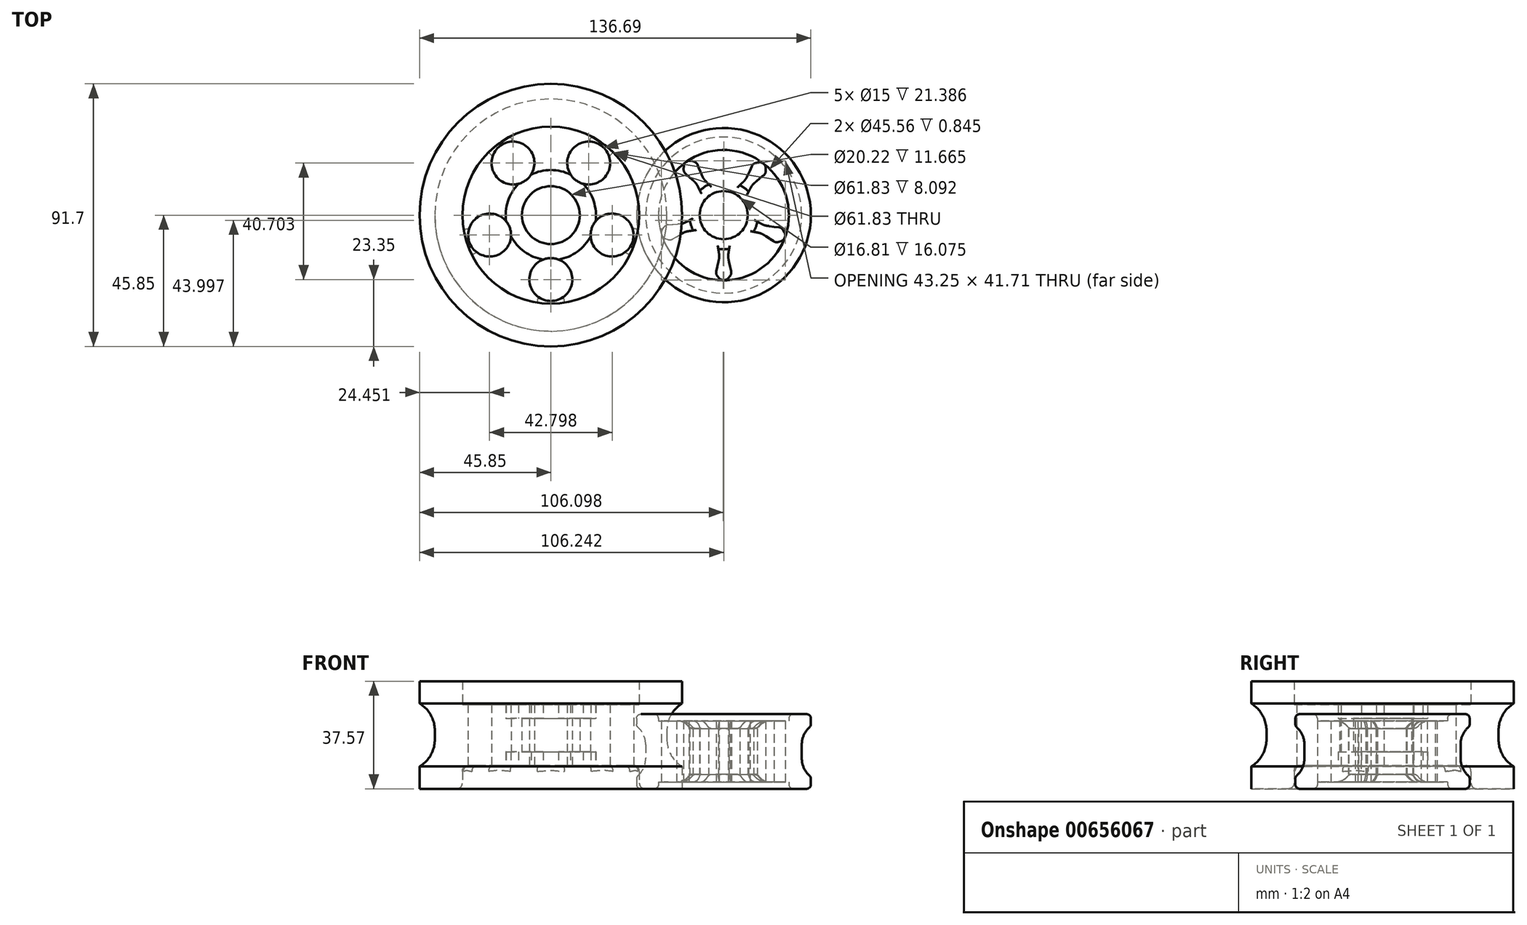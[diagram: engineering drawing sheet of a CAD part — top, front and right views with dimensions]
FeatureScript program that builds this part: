
annotation { "Feature Type Name" : "Feature", "Feature Type Description" : "" }
export const myFeature = defineFeature(function(context is Context, id is Id, definition is map)
    precondition{}
    {
        {
            var Q0;
            Q0=qCreatedBy(makeId("Front.planeOp"),FACE);
            var sketch = newSketch(context, id + "F0", { "sketchPlane" : qUnion([Q0])});
            skLineSegment(sketch, "E0", {"start": v(29.95, 21.08) * mm, "end": v(33.1, 21.08) * mm});
            skLineSegment(sketch, "E1", {"start": v(33.1, 21.08) * mm, "end": v(33.1, 5) * mm});
            skLineSegment(sketch, "E2", {"start": v(33.1, 5) * mm, "end": v(29.95, 5) * mm});
            skLineSegment(sketch, "E3", {"start": v(29.95, 5) * mm, "end": v(29.95, 0) * mm});
            skLineSegment(sketch, "E4", {"start": v(29.95, 0) * mm, "end": v(37.61, 0) * mm});
            skLineSegment(sketch, "E5", {"start": v(37.61, 0) * mm, "end": v(37.61, 2.35) * mm});
            skLineSegment(sketch, "E6", {"start": v(37.61, 2.35) * mm, "end": v(48.45, 2.35) * mm});
            skLineSegment(sketch, "E7", {"start": v(48.45, 2.35) * mm, "end": v(48.45, 5) * mm});
            skLineSegment(sketch, "E8", {"start": v(48.45, 5) * mm, "end": v(51.99, 5) * mm});
            skLineSegment(sketch, "E9", {"start": v(33.1, 13.04) * mm, "end": v(60.4, 13.04) * mm, "construction": true});
            skLineSegment(sketch, "E10.MirrorCS", {"start": v(37.61, 23.73) * mm, "end": v(48.45, 23.73) * mm});
            skLineSegment(sketch, "E11.MirrorCS", {"start": v(48.45, 21.08) * mm, "end": v(51.99, 21.08) * mm});
            skLineSegment(sketch, "E12.MirrorCS", {"start": v(48.45, 23.73) * mm, "end": v(48.45, 21.08) * mm});
            skLineSegment(sketch, "E13.MirrorCS", {"start": v(37.61, 26.08) * mm, "end": v(37.61, 23.73) * mm});
            skLineSegment(sketch, "E14.MirrorCS", {"start": v(29.95, 26.08) * mm, "end": v(37.61, 26.08) * mm});
            skLineSegment(sketch, "E15.MirrorCS", {"start": v(29.95, 21.08) * mm, "end": v(29.95, 26.08) * mm});
            skLineSegment(sketch, "E16", {"start": v(51.99, 21.08) * mm, "end": v(51.99, 5) * mm});
            skLineSegment(sketch, "E17", {"start": v(60.4, -28.23) * mm, "end": v(60.4, 48.4) * mm, "construction": true});
            skSolve(sketch);
        }
        {
            var Q0;
            Q0=makeQuery(id+"F0.imprint","IMPRINT",FACE,{"disambiguationData":[TD([[makeQuery(id+"F0.imprint","IMPRINT",EDGE,{"derivedFrom":sQuery(id+"F0.wireOp",EDGE,"E0")}),1.0]])]});
            var Q1;
            Q1=sQuery(id+"F0.wireOp",EDGE,"E17");
            revolve(context, id + "F1", {"entities" : qUnion([Q0]), "axis" : qUnion([Q1]), "revolveType" : RevolveType.FULL});
        }
        {
            var Q0;
            Q0=makeQuery(id+"F1.opRevolve","SWEPT_EDGE",EDGE,{"disambiguationData":[OSD([sQuery(id+"F0.wireOp",EDGE,"E0"),sQuery(id+"F0.wireOp",EDGE,"E15.MirrorCS")])]});
            var Q1;
            Q1=makeQuery(id+"F1.opRevolve","SWEPT_EDGE",EDGE,{"disambiguationData":[OSD([sQuery(id+"F0.wireOp",EDGE,"E14.MirrorCS"),sQuery(id+"F0.wireOp",EDGE,"E15.MirrorCS")])]});
            var Q2;
            Q2=makeQuery(id+"F1.opRevolve","SWEPT_EDGE",EDGE,{"disambiguationData":[OSD([sQuery(id+"F0.wireOp",EDGE,"E2"),sQuery(id+"F0.wireOp",EDGE,"E3")])]});
            var Q3;
            Q3=makeQuery(id+"F1.opRevolve","SWEPT_EDGE",EDGE,{"disambiguationData":[OSD([sQuery(id+"F0.wireOp",EDGE,"E3"),sQuery(id+"F0.wireOp",EDGE,"E4")])]});
            var Q4;
            Q4=makeQuery(id+"F1.opRevolve","SWEPT_EDGE",EDGE,{"disambiguationData":[OSD([sQuery(id+"F0.wireOp",EDGE,"E4"),sQuery(id+"F0.wireOp",EDGE,"E5")])]});
            var Q5;
            Q5=makeQuery(id+"F1.opRevolve","SWEPT_EDGE",EDGE,{"disambiguationData":[OSD([sQuery(id+"F0.wireOp",EDGE,"E13.MirrorCS"),sQuery(id+"F0.wireOp",EDGE,"E14.MirrorCS")])]});
            fillet(context, id + "F2", {"entities" : qUnion([Q0, Q1, Q2, Q3, Q4, Q5]), "radius" : 1.5 * mm, "tangentPropagation" : true, "allowEdgeOverflow" : false});
        }
        {
            var Q0;
            Q0=makeQuery(id+"F1.opRevolve","SWEPT_EDGE",EDGE,{"disambiguationData":[OSD([sQuery(id+"F0.wireOp",EDGE,"E1"),sQuery(id+"F0.wireOp",EDGE,"E2")])]});
            var Q1;
            Q1=makeQuery(id+"F1.opRevolve","SWEPT_EDGE",EDGE,{"disambiguationData":[OSD([sQuery(id+"F0.wireOp",EDGE,"E0"),sQuery(id+"F0.wireOp",EDGE,"E1")])]});
            fillet(context, id + "F3", {"entities" : qUnion([Q0, Q1]), "radius" : 8 * mm, "tangentPropagation" : true, "allowEdgeOverflow" : false});
        }
        {
            var Q0;
            Q0=qCreatedBy(makeId("Top.planeOp"),FACE);
            var sketch = newSketch(context, id + "F4", { "sketchPlane" : qUnion([Q0])});
            skArc(sketch, "E18", {"start": v(58.5, -11.8) * mm, "mid": v(60.4, -11.95) * mm, "end": v(62.29, -11.8) * mm});
            skLineSegment(sketch, "E19", {"start": v(60.4, 0) * mm, "end": v(60.4, -26.79) * mm, "construction": true});
            skLineSegment(sketch, "E20", {"start": v(58.5, -11.8) * mm, "end": v(58.78, -13.59) * mm});
            skLineSegment(sketch, "E21", {"start": v(58.73, -15.4) * mm, "end": v(58.2, -17.86) * mm});
            skLineSegment(sketch, "E22", {"start": v(58.18, -21.25) * mm, "end": v(58.77, -21.98) * mm});
            skLineSegment(sketch, "E23", {"start": v(58.15, -18.08) * mm, "end": v(57.79, -19.48) * mm});
            skLineSegment(sketch, "E24", {"start": v(60.32, -22.7) * mm, "end": v(60.4, -22.7) * mm});
            skPoint(sketch, "E25.visualSharp", {"position": v(59.37, -22.7) * mm});
            skArc(sketch, "E25.filletArc", {"start": v(58.77, -21.98) * mm, "mid": v(59.46, -22.52) * mm, "end": v(60.32, -22.7) * mm});
            skPoint(sketch, "E26.visualSharp", {"position": v(57.53, -20.46) * mm});
            skArc(sketch, "E26.filletArc", {"start": v(57.79, -19.48) * mm, "mid": v(57.77, -20.4) * mm, "end": v(58.18, -21.25) * mm});
            skPoint(sketch, "E27.visualSharp", {"position": v(58.92, -14.5) * mm});
            skArc(sketch, "E27.filletArc", {"start": v(58.73, -15.4) * mm, "mid": v(58.83, -14.5) * mm, "end": v(58.78, -13.59) * mm});
            skLineSegment(sketch, "E28.MirrorCS", {"start": v(60.46, -22.7) * mm, "end": v(60.4, -22.7) * mm});
            skLineSegment(sketch, "E29.MirrorCS", {"start": v(62.6, -21.25) * mm, "end": v(62.01, -21.98) * mm});
            skArc(sketch, "E30.MirrorCS", {"start": v(63, -19.48) * mm, "mid": v(63.01, -20.4) * mm, "end": v(62.6, -21.25) * mm});
            skArc(sketch, "E31.MirrorCS", {"start": v(62.01, -21.98) * mm, "mid": v(61.32, -22.52) * mm, "end": v(60.46, -22.7) * mm});
            skArc(sketch, "E32.MirrorCS", {"start": v(62.06, -15.4) * mm, "mid": v(61.95, -14.5) * mm, "end": v(62, -13.59) * mm});
            skLineSegment(sketch, "E33.MirrorCS", {"start": v(62.06, -15.4) * mm, "end": v(62.6, -17.97) * mm});
            skLineSegment(sketch, "E34.MirrorCS", {"start": v(62.29, -11.8) * mm, "end": v(62, -13.59) * mm});
            skLineSegment(sketch, "E35.MirrorCS", {"start": v(62.6, -17.97) * mm, "end": v(63, -19.48) * mm});
            skPoint(sketch, "E36.MirrorP", {"position": v(61.87, -14.5) * mm});
            skPoint(sketch, "E37.MirrorP", {"position": v(63.25, -20.46) * mm});
            skPoint(sketch, "E38.MirrorP", {"position": v(61.41, -22.7) * mm});
            skPoint(sketch, "E39.visualSharp", {"position": v(58.18, -17.97) * mm});
            skArc(sketch, "E39.filletArc", {"start": v(58.15, -18.08) * mm, "mid": v(58.18, -17.97) * mm, "end": v(58.2, -17.86) * mm});
            skCircle(sketch, "E40", {"center": v(60.4, 0) * mm, "radius": 11.95 * mm, "construction": true});
            skLineSegment(sketch, "E41.1.0", {"start": v(48.57, -1.74) * mm, "end": v(46.95, -2.55) * mm});
            skLineSegment(sketch, "E41.1.1", {"start": v(42.47, -3.3) * mm, "end": v(41.03, -3.37) * mm});
            skLineSegment(sketch, "E41.1.2", {"start": v(45.2, -3.04) * mm, "end": v(42.7, -3.28) * mm});
            skPoint(sketch, "E41.1.3", {"position": v(41.74, -8.88) * mm});
            skArc(sketch, "E41.1.4", {"start": v(48.57, -1.74) * mm, "mid": v(49, -3.6) * mm, "end": v(49.71, -5.35) * mm});
            skPoint(sketch, "E41.1.5", {"position": v(42.58, -3.3) * mm});
            skLineSegment(sketch, "E41.1.6", {"start": v(43.91, -7.51) * mm, "end": v(42.6, -8.34) * mm});
            skLineSegment(sketch, "E41.1.7", {"start": v(46.2, -6.22) * mm, "end": v(43.91, -7.51) * mm});
            skPoint(sketch, "E41.1.8", {"position": v(39.04, -7.8) * mm});
            skPoint(sketch, "E41.1.9", {"position": v(38.43, -5.86) * mm});
            skLineSegment(sketch, "E41.1.10", {"start": v(49.71, -5.35) * mm, "end": v(47.92, -5.63) * mm});
            skPoint(sketch, "E41.1.11", {"position": v(47, -5.77) * mm});
            skPoint(sketch, "E41.1.12", {"position": v(46.12, -2.95) * mm});
            skPoint(sketch, "E41.1.13", {"position": v(40.02, -3.43) * mm});
            skArc(sketch, "E41.1.14", {"start": v(41.03, -3.37) * mm, "mid": v(40.14, -3.64) * mm, "end": v(39.46, -4.28) * mm});
            skArc(sketch, "E41.1.15", {"start": v(38.95, -5.06) * mm, "mid": v(38.64, -5.89) * mm, "end": v(38.71, -6.76) * mm});
            skArc(sketch, "E41.1.16", {"start": v(39.92, -8.15) * mm, "mid": v(39.2, -7.66) * mm, "end": v(38.76, -6.9) * mm});
            skArc(sketch, "E41.1.17", {"start": v(46.2, -6.22) * mm, "mid": v(47.04, -5.84) * mm, "end": v(47.92, -5.63) * mm});
            skArc(sketch, "E41.1.18", {"start": v(45.2, -3.04) * mm, "mid": v(46.1, -2.87) * mm, "end": v(46.95, -2.55) * mm});
            skArc(sketch, "E41.1.19", {"start": v(42.6, -8.34) * mm, "mid": v(41.72, -8.64) * mm, "end": v(40.8, -8.5) * mm});
            skLineSegment(sketch, "E41.1.20", {"start": v(40.8, -8.5) * mm, "end": v(39.92, -8.15) * mm});
            skLineSegment(sketch, "E41.1.21", {"start": v(39.46, -4.28) * mm, "end": v(38.95, -5.06) * mm});
            skArc(sketch, "E41.1.22", {"start": v(42.47, -3.3) * mm, "mid": v(42.58, -3.3) * mm, "end": v(42.7, -3.28) * mm});
            skLineSegment(sketch, "E41.1.23", {"start": v(38.76, -6.9) * mm, "end": v(38.73, -6.83) * mm});
            skLineSegment(sketch, "E41.1.24", {"start": v(38.71, -6.76) * mm, "end": v(38.73, -6.83) * mm});
            skLineSegment(sketch, "E41.2.0", {"start": v(55.18, 10.75) * mm, "end": v(53.92, 12.06) * mm});
            skLineSegment(sketch, "E41.2.1", {"start": v(51.86, 16.1) * mm, "end": v(51.35, 17.45) * mm});
            skLineSegment(sketch, "E41.2.2", {"start": v(52.92, 13.57) * mm, "end": v(51.94, 15.89) * mm});
            skPoint(sketch, "E41.2.3", {"position": v(46.31, 15.12) * mm});
            skArc(sketch, "E41.2.4", {"start": v(55.18, 10.75) * mm, "mid": v(53.54, 9.79) * mm, "end": v(52.07, 8.57) * mm});
            skPoint(sketch, "E41.2.5", {"position": v(51.9, 16) * mm});
            skLineSegment(sketch, "E41.2.6", {"start": v(48.27, 13.45) * mm, "end": v(47.09, 14.46) * mm});
            skLineSegment(sketch, "E41.2.7", {"start": v(50.2, 11.66) * mm, "end": v(48.27, 13.45) * mm});
            skPoint(sketch, "E41.2.8", {"position": v(46.53, 18.02) * mm});
            skPoint(sketch, "E41.2.9", {"position": v(48.2, 19.19) * mm});
            skLineSegment(sketch, "E41.2.10", {"start": v(52.07, 8.57) * mm, "end": v(51.27, 10.2) * mm});
            skPoint(sketch, "E41.2.11", {"position": v(50.87, 11.03) * mm});
            skPoint(sketch, "E41.2.12", {"position": v(53.28, 12.72) * mm});
            skPoint(sketch, "E41.2.13", {"position": v(51, 18.4) * mm});
            skArc(sketch, "E41.2.14", {"start": v(51.35, 17.45) * mm, "mid": v(50.83, 18.22) * mm, "end": v(50.02, 18.68) * mm});
            skArc(sketch, "E41.2.15", {"start": v(49.11, 18.93) * mm, "mid": v(48.24, 18.98) * mm, "end": v(47.43, 18.64) * mm});
            skArc(sketch, "E41.2.16", {"start": v(46.46, 17.07) * mm, "mid": v(46.72, 17.91) * mm, "end": v(47.3, 18.56) * mm});
            skArc(sketch, "E41.2.17", {"start": v(50.2, 11.66) * mm, "mid": v(50.8, 10.98) * mm, "end": v(51.27, 10.2) * mm});
            skArc(sketch, "E41.2.18", {"start": v(52.92, 13.57) * mm, "mid": v(53.35, 12.77) * mm, "end": v(53.92, 12.06) * mm});
            skArc(sketch, "E41.2.19", {"start": v(47.09, 14.46) * mm, "mid": v(46.54, 15.21) * mm, "end": v(46.39, 16.13) * mm});
            skLineSegment(sketch, "E41.2.20", {"start": v(46.39, 16.13) * mm, "end": v(46.46, 17.07) * mm});
            skLineSegment(sketch, "E41.2.21", {"start": v(50.02, 18.68) * mm, "end": v(49.11, 18.93) * mm});
            skArc(sketch, "E41.2.22", {"start": v(51.86, 16.1) * mm, "mid": v(51.9, 16) * mm, "end": v(51.94, 15.89) * mm});
            skLineSegment(sketch, "E41.2.23", {"start": v(47.3, 18.56) * mm, "end": v(47.37, 18.6) * mm});
            skLineSegment(sketch, "E41.2.24", {"start": v(47.43, 18.64) * mm, "end": v(47.37, 18.6) * mm});
            skLineSegment(sketch, "E41.3.0", {"start": v(69.08, 8.2) * mm, "end": v(69.95, 9.8) * mm});
            skLineSegment(sketch, "E41.3.1", {"start": v(73.18, 12.98) * mm, "end": v(74.31, 13.87) * mm});
            skLineSegment(sketch, "E41.3.2", {"start": v(71.09, 11.2) * mm, "end": v(73, 12.84) * mm});
            skPoint(sketch, "E41.3.3", {"position": v(70.58, 17.97) * mm});
            skArc(sketch, "E41.3.4", {"start": v(69.08, 8.2) * mm, "mid": v(67.66, 9.48) * mm, "end": v(66.07, 10.51) * mm});
            skPoint(sketch, "E41.3.5", {"position": v(73.09, 12.91) * mm});
            skLineSegment(sketch, "E41.3.6", {"start": v(69.58, 15.6) * mm, "end": v(70.18, 17.04) * mm});
            skLineSegment(sketch, "E41.3.7", {"start": v(68.44, 13.23) * mm, "end": v(69.58, 15.6) * mm});
            skPoint(sketch, "E41.3.8", {"position": v(73.4, 18.64) * mm});
            skPoint(sketch, "E41.3.9", {"position": v(75.02, 17.4) * mm});
            skLineSegment(sketch, "E41.3.10", {"start": v(66.07, 10.51) * mm, "end": v(67.38, 11.76) * mm});
            skPoint(sketch, "E41.3.11", {"position": v(68.05, 12.4) * mm});
            skPoint(sketch, "E41.3.12", {"position": v(70.39, 10.6) * mm});
            skPoint(sketch, "E41.3.13", {"position": v(75.12, 14.5) * mm});
            skArc(sketch, "E41.3.14", {"start": v(74.31, 13.87) * mm, "mid": v(74.9, 14.6) * mm, "end": v(75.08, 15.5) * mm});
            skArc(sketch, "E41.3.15", {"start": v(75.05, 16.45) * mm, "mid": v(74.83, 17.3) * mm, "end": v(74.27, 17.97) * mm});
            skArc(sketch, "E41.3.16", {"start": v(72.48, 18.42) * mm, "mid": v(73.36, 18.43) * mm, "end": v(74.16, 18.06) * mm});
            skArc(sketch, "E41.3.17", {"start": v(68.44, 13.23) * mm, "mid": v(67.98, 12.45) * mm, "end": v(67.38, 11.76) * mm});
            skArc(sketch, "E41.3.18", {"start": v(71.09, 11.2) * mm, "mid": v(70.45, 10.55) * mm, "end": v(69.95, 9.8) * mm});
            skArc(sketch, "E41.3.19", {"start": v(70.18, 17.04) * mm, "mid": v(70.74, 17.79) * mm, "end": v(71.57, 18.2) * mm});
            skLineSegment(sketch, "E41.3.20", {"start": v(71.57, 18.2) * mm, "end": v(72.48, 18.42) * mm});
            skLineSegment(sketch, "E41.3.21", {"start": v(75.08, 15.5) * mm, "end": v(75.05, 16.45) * mm});
            skArc(sketch, "E41.3.22", {"start": v(73.18, 12.98) * mm, "mid": v(73.09, 12.91) * mm, "end": v(73, 12.84) * mm});
            skLineSegment(sketch, "E41.3.23", {"start": v(74.16, 18.06) * mm, "end": v(74.22, 18.02) * mm});
            skLineSegment(sketch, "E41.3.24", {"start": v(74.27, 17.97) * mm, "end": v(74.22, 18.02) * mm});
            skLineSegment(sketch, "E41.4.0", {"start": v(70.83, -5.81) * mm, "end": v(72.6, -6.17) * mm});
            skLineSegment(sketch, "E41.4.1", {"start": v(76.62, -8.3) * mm, "end": v(77.8, -9.1) * mm});
            skLineSegment(sketch, "E41.4.2", {"start": v(74.3, -6.83) * mm, "end": v(76.43, -8.17) * mm});
            skPoint(sketch, "E41.4.3", {"position": v(80.6, -4.31) * mm});
            skArc(sketch, "E41.4.4", {"start": v(70.83, -5.81) * mm, "mid": v(71.62, -4.09) * mm, "end": v(72.12, -2.25) * mm});
            skPoint(sketch, "E41.4.5", {"position": v(76.52, -8.23) * mm});
            skLineSegment(sketch, "E41.4.6", {"start": v(78.04, -4.07) * mm, "end": v(79.58, -4.22) * mm});
            skLineSegment(sketch, "E41.4.7", {"start": v(75.43, -3.7) * mm, "end": v(78.04, -4.07) * mm});
            skPoint(sketch, "E41.4.8", {"position": v(82.08, -6.8) * mm});
            skPoint(sketch, "E41.4.9", {"position": v(81.38, -8.72) * mm});
            skLineSegment(sketch, "E41.4.10", {"start": v(72.12, -2.25) * mm, "end": v(73.71, -3.13) * mm});
            skPoint(sketch, "E41.4.11", {"position": v(74.52, -3.57) * mm});
            skPoint(sketch, "E41.4.12", {"position": v(73.51, -6.34) * mm});
            skPoint(sketch, "E41.4.13", {"position": v(78.64, -9.69) * mm});
            skArc(sketch, "E41.4.14", {"start": v(77.8, -9.1) * mm, "mid": v(78.67, -9.44) * mm, "end": v(79.6, -9.35) * mm});
            skArc(sketch, "E41.4.15", {"start": v(80.49, -9.04) * mm, "mid": v(81.23, -8.57) * mm, "end": v(81.7, -7.83) * mm});
            skArc(sketch, "E41.4.16", {"start": v(81.6, -6) * mm, "mid": v(81.87, -6.83) * mm, "end": v(81.76, -7.7) * mm});
            skArc(sketch, "E41.4.17", {"start": v(75.43, -3.7) * mm, "mid": v(74.55, -3.5) * mm, "end": v(73.71, -3.13) * mm});
            skArc(sketch, "E41.4.18", {"start": v(74.3, -6.83) * mm, "mid": v(73.48, -6.42) * mm, "end": v(72.6, -6.17) * mm});
            skArc(sketch, "E41.4.19", {"start": v(79.58, -4.22) * mm, "mid": v(80.47, -4.52) * mm, "end": v(81.12, -5.19) * mm});
            skLineSegment(sketch, "E41.4.20", {"start": v(81.12, -5.19) * mm, "end": v(81.6, -6) * mm});
            skLineSegment(sketch, "E41.4.21", {"start": v(79.6, -9.35) * mm, "end": v(80.49, -9.04) * mm});
            skArc(sketch, "E41.4.22", {"start": v(76.62, -8.3) * mm, "mid": v(76.52, -8.23) * mm, "end": v(76.43, -8.17) * mm});
            skLineSegment(sketch, "E41.4.23", {"start": v(81.76, -7.7) * mm, "end": v(81.73, -7.77) * mm});
            skLineSegment(sketch, "E41.4.24", {"start": v(81.7, -7.83) * mm, "end": v(81.73, -7.77) * mm});
            skLineSegment(sketch, "E41.anchor1", {"start": v(60.4, 0) * mm, "end": v(53.31, -16.82) * mm, "construction": true});
            skLineSegment(sketch, "E41.anchor2", {"start": v(60.4, 0) * mm, "end": v(73.78, -12.4) * mm, "construction": true});
            skSolve(sketch);
        }
        {
            var Q0;
            Q0 = qSketchRegion(id + "F4", true);
            extrude(context, id + "F5", {"entities" : qUnion([Q0]), "operationType" : NewBodyOperationType.REMOVE, "depth" : 89.9 * mm, "offsetDistance" : 25 * mm});
        }
        {
            var Q0;
            {var subQ0=sQuery(id+"F0.wireOp",EDGE,"E6");var subQ1=sQuery(id+"F0.wireOp",EDGE,"E7");Q0=makeQuery(id+"F5.boolean.opBoolean","SPLIT",EDGE,{"disambiguationData":[TD([makeQuery(id+"F5.opExtrude","SWEPT_FACE",FACE,{"disambiguationData":[OSD([sQuery(id+"F4.wireOp",EDGE,"E41.1.0")])]})])],"derivedFrom":makeQuery(id+"F1.opRevolve","SWEPT_EDGE",EDGE,{"disambiguationData":[OSD([subQ0,subQ1])]})});}
            var Q1;
            {var subQ0=sQuery(id+"F0.wireOp",EDGE,"E6");var subQ1=sQuery(id+"F0.wireOp",EDGE,"E7");Q1=makeQuery(id+"F5.boolean.opBoolean","SPLIT",EDGE,{"disambiguationData":[TD([makeQuery(id+"F5.opExtrude","SWEPT_FACE",FACE,{"disambiguationData":[OSD([sQuery(id+"F4.wireOp",EDGE,"E20")])]})])],"derivedFrom":makeQuery(id+"F1.opRevolve","SWEPT_EDGE",EDGE,{"disambiguationData":[OSD([subQ0,subQ1])]})});}
            var Q2;
            {var subQ0=sQuery(id+"F0.wireOp",EDGE,"E6");var subQ1=sQuery(id+"F0.wireOp",EDGE,"E7");Q2=makeQuery(id+"F5.boolean.opBoolean","SPLIT",EDGE,{"disambiguationData":[TD([makeQuery(id+"F5.opExtrude","SWEPT_FACE",FACE,{"disambiguationData":[OSD([sQuery(id+"F4.wireOp",EDGE,"E41.2.0")])]})])],"derivedFrom":makeQuery(id+"F1.opRevolve","SWEPT_EDGE",EDGE,{"disambiguationData":[OSD([subQ0,subQ1])]})});}
            var Q3;
            {var subQ0=sQuery(id+"F0.wireOp",EDGE,"E6");var subQ1=sQuery(id+"F0.wireOp",EDGE,"E7");Q3=makeQuery(id+"F5.boolean.opBoolean","SPLIT",EDGE,{"disambiguationData":[TD([makeQuery(id+"F5.opExtrude","SWEPT_FACE",FACE,{"disambiguationData":[OSD([sQuery(id+"F4.wireOp",EDGE,"E41.3.0")])]})])],"derivedFrom":makeQuery(id+"F1.opRevolve","SWEPT_EDGE",EDGE,{"disambiguationData":[OSD([subQ0,subQ1])]})});}
            var Q4;
            {var subQ0=sQuery(id+"F0.wireOp",EDGE,"E6");var subQ1=sQuery(id+"F0.wireOp",EDGE,"E7");Q4=makeQuery(id+"F5.boolean.opBoolean","SPLIT",EDGE,{"disambiguationData":[TD([makeQuery(id+"F5.opExtrude","SWEPT_FACE",FACE,{"disambiguationData":[OSD([sQuery(id+"F4.wireOp",EDGE,"E34.MirrorCS")])]})])],"derivedFrom":makeQuery(id+"F1.opRevolve","SWEPT_EDGE",EDGE,{"disambiguationData":[OSD([subQ0,subQ1])]})});}
            var Q5;
            {var subQ0=sQuery(id+"F0.wireOp",EDGE,"E10.MirrorCS");var subQ1=sQuery(id+"F0.wireOp",EDGE,"E12.MirrorCS");Q5=makeQuery(id+"F5.boolean.opBoolean","SPLIT",EDGE,{"disambiguationData":[TD([makeQuery(id+"F5.opExtrude","SWEPT_FACE",FACE,{"disambiguationData":[OSD([sQuery(id+"F4.wireOp",EDGE,"E41.2.0")])]})])],"derivedFrom":makeQuery(id+"F1.opRevolve","SWEPT_EDGE",EDGE,{"disambiguationData":[OSD([subQ0,subQ1])]})});}
            var Q6;
            {var subQ0=sQuery(id+"F0.wireOp",EDGE,"E10.MirrorCS");var subQ1=sQuery(id+"F0.wireOp",EDGE,"E12.MirrorCS");Q6=makeQuery(id+"F5.boolean.opBoolean","SPLIT",EDGE,{"disambiguationData":[TD([makeQuery(id+"F5.opExtrude","SWEPT_FACE",FACE,{"disambiguationData":[OSD([sQuery(id+"F4.wireOp",EDGE,"E41.3.0")])]})])],"derivedFrom":makeQuery(id+"F1.opRevolve","SWEPT_EDGE",EDGE,{"disambiguationData":[OSD([subQ0,subQ1])]})});}
            var Q7;
            {var subQ0=sQuery(id+"F0.wireOp",EDGE,"E10.MirrorCS");var subQ1=sQuery(id+"F0.wireOp",EDGE,"E12.MirrorCS");Q7=makeQuery(id+"F5.boolean.opBoolean","SPLIT",EDGE,{"disambiguationData":[TD([makeQuery(id+"F5.opExtrude","SWEPT_FACE",FACE,{"disambiguationData":[OSD([sQuery(id+"F4.wireOp",EDGE,"E41.1.0")])]})])],"derivedFrom":makeQuery(id+"F1.opRevolve","SWEPT_EDGE",EDGE,{"disambiguationData":[OSD([subQ0,subQ1])]})});}
            var Q8;
            {var subQ0=sQuery(id+"F0.wireOp",EDGE,"E10.MirrorCS");var subQ1=sQuery(id+"F0.wireOp",EDGE,"E12.MirrorCS");Q8=makeQuery(id+"F5.boolean.opBoolean","SPLIT",EDGE,{"disambiguationData":[TD([makeQuery(id+"F5.opExtrude","SWEPT_FACE",FACE,{"disambiguationData":[OSD([sQuery(id+"F4.wireOp",EDGE,"E20")])]})])],"derivedFrom":makeQuery(id+"F1.opRevolve","SWEPT_EDGE",EDGE,{"disambiguationData":[OSD([subQ0,subQ1])]})});}
            var Q9;
            {var subQ0=sQuery(id+"F0.wireOp",EDGE,"E10.MirrorCS");var subQ1=sQuery(id+"F0.wireOp",EDGE,"E12.MirrorCS");Q9=makeQuery(id+"F5.boolean.opBoolean","SPLIT",EDGE,{"disambiguationData":[TD([makeQuery(id+"F5.opExtrude","SWEPT_FACE",FACE,{"disambiguationData":[OSD([sQuery(id+"F4.wireOp",EDGE,"E34.MirrorCS")])]})])],"derivedFrom":makeQuery(id+"F1.opRevolve","SWEPT_EDGE",EDGE,{"disambiguationData":[OSD([subQ0,subQ1])]})});}
            fillet(context, id + "F6", {"entities" : qUnion([Q0, Q1, Q2, Q3, Q4, Q5, Q6, Q7, Q8, Q9]), "radius" : 5 * mm, "tangentPropagation" : true, "allowEdgeOverflow" : false});
        }
        {
            var Q0;
            {var subQ0=sQuery(id+"F0.wireOp",EDGE,"E10.MirrorCS");var subQ1=sQuery(id+"F0.wireOp",EDGE,"E12.MirrorCS");Q0=makeQuery(id+"F6.opFillet","BLEND_EDGE",EDGE,{"blendedFrom":[makeQuery(id+"F5.boolean.opBoolean","SPLIT",EDGE,{"disambiguationData":[TD([makeQuery(id+"F5.opExtrude","SWEPT_FACE",FACE,{"disambiguationData":[OSD([sQuery(id+"F4.wireOp",EDGE,"E41.2.0")])]})])],"derivedFrom":makeQuery(id+"F1.opRevolve","SWEPT_EDGE",EDGE,{"disambiguationData":[OSD([subQ0,subQ1])]})}),makeQuery(id+"F1.opRevolve","SWEPT_FACE",FACE,{"disambiguationData":[OSD([sQuery(id+"F0.wireOp",EDGE,"E11.MirrorCS")])]})],"blendedInto":[makeQuery(id+"F1.opRevolve","SWEPT_FACE",FACE,{"disambiguationData":[OSD([sQuery(id+"F0.wireOp",EDGE,"E11.MirrorCS")])]})]});}
            var Q1;
            {var subQ0=sQuery(id+"F0.wireOp",EDGE,"E10.MirrorCS");var subQ1=sQuery(id+"F0.wireOp",EDGE,"E12.MirrorCS");Q1=makeQuery(id+"F6.opFillet","BLEND_EDGE",EDGE,{"blendedFrom":[makeQuery(id+"F5.boolean.opBoolean","SPLIT",EDGE,{"disambiguationData":[TD([makeQuery(id+"F5.opExtrude","SWEPT_FACE",FACE,{"disambiguationData":[OSD([sQuery(id+"F4.wireOp",EDGE,"E41.3.0")])]})])],"derivedFrom":makeQuery(id+"F1.opRevolve","SWEPT_EDGE",EDGE,{"disambiguationData":[OSD([subQ0,subQ1])]})}),makeQuery(id+"F1.opRevolve","SWEPT_FACE",FACE,{"disambiguationData":[OSD([sQuery(id+"F0.wireOp",EDGE,"E11.MirrorCS")])]})],"blendedInto":[makeQuery(id+"F1.opRevolve","SWEPT_FACE",FACE,{"disambiguationData":[OSD([sQuery(id+"F0.wireOp",EDGE,"E11.MirrorCS")])]})]});}
            var Q2;
            {var subQ0=sQuery(id+"F0.wireOp",EDGE,"E10.MirrorCS");var subQ1=sQuery(id+"F0.wireOp",EDGE,"E12.MirrorCS");Q2=makeQuery(id+"F6.opFillet","BLEND_EDGE",EDGE,{"blendedFrom":[makeQuery(id+"F5.boolean.opBoolean","SPLIT",EDGE,{"disambiguationData":[TD([makeQuery(id+"F5.opExtrude","SWEPT_FACE",FACE,{"disambiguationData":[OSD([sQuery(id+"F4.wireOp",EDGE,"E41.1.0")])]})])],"derivedFrom":makeQuery(id+"F1.opRevolve","SWEPT_EDGE",EDGE,{"disambiguationData":[OSD([subQ0,subQ1])]})}),makeQuery(id+"F1.opRevolve","SWEPT_FACE",FACE,{"disambiguationData":[OSD([sQuery(id+"F0.wireOp",EDGE,"E11.MirrorCS")])]})],"blendedInto":[makeQuery(id+"F1.opRevolve","SWEPT_FACE",FACE,{"disambiguationData":[OSD([sQuery(id+"F0.wireOp",EDGE,"E11.MirrorCS")])]})]});}
            var Q3;
            {var subQ0=sQuery(id+"F0.wireOp",EDGE,"E10.MirrorCS");var subQ1=sQuery(id+"F0.wireOp",EDGE,"E12.MirrorCS");Q3=makeQuery(id+"F6.opFillet","BLEND_EDGE",EDGE,{"blendedFrom":[makeQuery(id+"F5.boolean.opBoolean","SPLIT",EDGE,{"disambiguationData":[TD([makeQuery(id+"F5.opExtrude","SWEPT_FACE",FACE,{"disambiguationData":[OSD([sQuery(id+"F4.wireOp",EDGE,"E20")])]})])],"derivedFrom":makeQuery(id+"F1.opRevolve","SWEPT_EDGE",EDGE,{"disambiguationData":[OSD([subQ0,subQ1])]})}),makeQuery(id+"F1.opRevolve","SWEPT_FACE",FACE,{"disambiguationData":[OSD([sQuery(id+"F0.wireOp",EDGE,"E11.MirrorCS")])]})],"blendedInto":[makeQuery(id+"F1.opRevolve","SWEPT_FACE",FACE,{"disambiguationData":[OSD([sQuery(id+"F0.wireOp",EDGE,"E11.MirrorCS")])]})]});}
            var Q4;
            {var subQ0=sQuery(id+"F0.wireOp",EDGE,"E10.MirrorCS");var subQ1=sQuery(id+"F0.wireOp",EDGE,"E12.MirrorCS");Q4=makeQuery(id+"F6.opFillet","BLEND_EDGE",EDGE,{"blendedFrom":[makeQuery(id+"F5.boolean.opBoolean","SPLIT",EDGE,{"disambiguationData":[TD([makeQuery(id+"F5.opExtrude","SWEPT_FACE",FACE,{"disambiguationData":[OSD([sQuery(id+"F4.wireOp",EDGE,"E34.MirrorCS")])]})])],"derivedFrom":makeQuery(id+"F1.opRevolve","SWEPT_EDGE",EDGE,{"disambiguationData":[OSD([subQ0,subQ1])]})}),makeQuery(id+"F1.opRevolve","SWEPT_FACE",FACE,{"disambiguationData":[OSD([sQuery(id+"F0.wireOp",EDGE,"E11.MirrorCS")])]})],"blendedInto":[makeQuery(id+"F1.opRevolve","SWEPT_FACE",FACE,{"disambiguationData":[OSD([sQuery(id+"F0.wireOp",EDGE,"E11.MirrorCS")])]})]});}
            var Q5;
            {var subQ0=sQuery(id+"F0.wireOp",EDGE,"E6");var subQ1=sQuery(id+"F0.wireOp",EDGE,"E7");Q5=makeQuery(id+"F6.opFillet","BLEND_EDGE",EDGE,{"blendedFrom":[makeQuery(id+"F5.boolean.opBoolean","SPLIT",EDGE,{"disambiguationData":[TD([makeQuery(id+"F5.opExtrude","SWEPT_FACE",FACE,{"disambiguationData":[OSD([sQuery(id+"F4.wireOp",EDGE,"E20")])]})])],"derivedFrom":makeQuery(id+"F1.opRevolve","SWEPT_EDGE",EDGE,{"disambiguationData":[OSD([subQ0,subQ1])]})}),makeQuery(id+"F1.opRevolve","SWEPT_FACE",FACE,{"disambiguationData":[OSD([sQuery(id+"F0.wireOp",EDGE,"E8")])]})],"blendedInto":[makeQuery(id+"F1.opRevolve","SWEPT_FACE",FACE,{"disambiguationData":[OSD([sQuery(id+"F0.wireOp",EDGE,"E8")])]})]});}
            var Q6;
            {var subQ0=sQuery(id+"F0.wireOp",EDGE,"E6");var subQ1=sQuery(id+"F0.wireOp",EDGE,"E7");Q6=makeQuery(id+"F6.opFillet","BLEND_EDGE",EDGE,{"blendedFrom":[makeQuery(id+"F5.boolean.opBoolean","SPLIT",EDGE,{"disambiguationData":[TD([makeQuery(id+"F5.opExtrude","SWEPT_FACE",FACE,{"disambiguationData":[OSD([sQuery(id+"F4.wireOp",EDGE,"E34.MirrorCS")])]})])],"derivedFrom":makeQuery(id+"F1.opRevolve","SWEPT_EDGE",EDGE,{"disambiguationData":[OSD([subQ0,subQ1])]})}),makeQuery(id+"F1.opRevolve","SWEPT_FACE",FACE,{"disambiguationData":[OSD([sQuery(id+"F0.wireOp",EDGE,"E8")])]})],"blendedInto":[makeQuery(id+"F1.opRevolve","SWEPT_FACE",FACE,{"disambiguationData":[OSD([sQuery(id+"F0.wireOp",EDGE,"E8")])]})]});}
            var Q7;
            {var subQ0=sQuery(id+"F0.wireOp",EDGE,"E6");var subQ1=sQuery(id+"F0.wireOp",EDGE,"E7");Q7=makeQuery(id+"F6.opFillet","BLEND_EDGE",EDGE,{"blendedFrom":[makeQuery(id+"F5.boolean.opBoolean","SPLIT",EDGE,{"disambiguationData":[TD([makeQuery(id+"F5.opExtrude","SWEPT_FACE",FACE,{"disambiguationData":[OSD([sQuery(id+"F4.wireOp",EDGE,"E41.1.0")])]})])],"derivedFrom":makeQuery(id+"F1.opRevolve","SWEPT_EDGE",EDGE,{"disambiguationData":[OSD([subQ0,subQ1])]})}),makeQuery(id+"F1.opRevolve","SWEPT_FACE",FACE,{"disambiguationData":[OSD([sQuery(id+"F0.wireOp",EDGE,"E8")])]})],"blendedInto":[makeQuery(id+"F1.opRevolve","SWEPT_FACE",FACE,{"disambiguationData":[OSD([sQuery(id+"F0.wireOp",EDGE,"E8")])]})]});}
            var Q8;
            {var subQ0=sQuery(id+"F0.wireOp",EDGE,"E6");var subQ1=sQuery(id+"F0.wireOp",EDGE,"E7");Q8=makeQuery(id+"F6.opFillet","BLEND_EDGE",EDGE,{"blendedFrom":[makeQuery(id+"F5.boolean.opBoolean","SPLIT",EDGE,{"disambiguationData":[TD([makeQuery(id+"F5.opExtrude","SWEPT_FACE",FACE,{"disambiguationData":[OSD([sQuery(id+"F4.wireOp",EDGE,"E41.3.0")])]})])],"derivedFrom":makeQuery(id+"F1.opRevolve","SWEPT_EDGE",EDGE,{"disambiguationData":[OSD([subQ0,subQ1])]})}),makeQuery(id+"F1.opRevolve","SWEPT_FACE",FACE,{"disambiguationData":[OSD([sQuery(id+"F0.wireOp",EDGE,"E8")])]})],"blendedInto":[makeQuery(id+"F1.opRevolve","SWEPT_FACE",FACE,{"disambiguationData":[OSD([sQuery(id+"F0.wireOp",EDGE,"E8")])]})]});}
            var Q9;
            {var subQ0=sQuery(id+"F0.wireOp",EDGE,"E6");var subQ1=sQuery(id+"F0.wireOp",EDGE,"E7");Q9=makeQuery(id+"F6.opFillet","BLEND_EDGE",EDGE,{"blendedFrom":[makeQuery(id+"F5.boolean.opBoolean","SPLIT",EDGE,{"disambiguationData":[TD([makeQuery(id+"F5.opExtrude","SWEPT_FACE",FACE,{"disambiguationData":[OSD([sQuery(id+"F4.wireOp",EDGE,"E41.2.0")])]})])],"derivedFrom":makeQuery(id+"F1.opRevolve","SWEPT_EDGE",EDGE,{"disambiguationData":[OSD([subQ0,subQ1])]})}),makeQuery(id+"F1.opRevolve","SWEPT_FACE",FACE,{"disambiguationData":[OSD([sQuery(id+"F0.wireOp",EDGE,"E8")])]})],"blendedInto":[makeQuery(id+"F1.opRevolve","SWEPT_FACE",FACE,{"disambiguationData":[OSD([sQuery(id+"F0.wireOp",EDGE,"E8")])]})]});}
            fillet(context, id + "F7", {"entities" : qUnion([Q0, Q1, Q2, Q3, Q4, Q5, Q6, Q7, Q8, Q9]), "radius" : 2 * mm, "tangentPropagation" : true, "allowEdgeOverflow" : false});
        }
        {
            var Q0;
            Q0=qCreatedBy(makeId("Front.planeOp"),FACE);
            var sketch = newSketch(context, id + "F8", { "sketchPlane" : qUnion([Q0])});
            skLineSegment(sketch, "E42", {"start": v(-61.24, 18.79) * mm, "end": v(0, 18.79) * mm, "construction": true});
            skLineSegment(sketch, "E43", {"start": v(-10.1, 18.79) * mm, "end": v(-10.1, 24.62) * mm});
            skLineSegment(sketch, "E44", {"start": v(-10.1, 24.62) * mm, "end": v(-15.75, 24.62) * mm});
            skLineSegment(sketch, "E45", {"start": v(-15.75, 24.62) * mm, "end": v(-15.75, 29.48) * mm});
            skLineSegment(sketch, "E46", {"start": v(-15.75, 29.48) * mm, "end": v(-30.91, 29.48) * mm});
            skLineSegment(sketch, "E47", {"start": v(-30.91, 29.48) * mm, "end": v(-30.91, 37.57) * mm});
            skLineSegment(sketch, "E48", {"start": v(-30.91, 37.57) * mm, "end": v(-45.85, 37.57) * mm});
            skLineSegment(sketch, "E49", {"start": v(-45.85, 37.57) * mm, "end": v(-45.85, 29.8) * mm});
            skLineSegment(sketch, "E50", {"start": v(-45.85, 29.8) * mm, "end": v(-40.56, 29.8) * mm});
            skLineSegment(sketch, "E51", {"start": v(-40.56, 29.8) * mm, "end": v(-40.56, 18.79) * mm});
            skLineSegment(sketch, "E52.MirrorCS", {"start": v(-30.91, 8.1) * mm, "end": v(-30.91, 0) * mm});
            skLineSegment(sketch, "E53.MirrorCS", {"start": v(-15.75, 12.95) * mm, "end": v(-15.75, 8.1) * mm});
            skLineSegment(sketch, "E54.MirrorCS", {"start": v(-45.85, 7.77) * mm, "end": v(-40.56, 7.77) * mm});
            skLineSegment(sketch, "E55.MirrorCS", {"start": v(-10.1, 12.95) * mm, "end": v(-15.75, 12.95) * mm});
            skLineSegment(sketch, "E56.MirrorCS", {"start": v(-45.85, 0) * mm, "end": v(-45.85, 7.77) * mm});
            skLineSegment(sketch, "E57.MirrorCS", {"start": v(-40.56, 7.77) * mm, "end": v(-40.56, 18.79) * mm});
            skLineSegment(sketch, "E58.MirrorCS", {"start": v(-10.1, 18.79) * mm, "end": v(-10.1, 12.95) * mm});
            skLineSegment(sketch, "E59.MirrorCS", {"start": v(-30.91, 0) * mm, "end": v(-45.85, 0) * mm});
            skLineSegment(sketch, "E60.MirrorCS", {"start": v(-15.75, 8.1) * mm, "end": v(-30.91, 8.1) * mm});
            skLineSegment(sketch, "E61", {"start": v(0, 18.79) * mm, "end": v(0, 61.21) * mm, "construction": true});
            skLineSegment(sketch, "E62", {"start": v(-30.91, 0) * mm, "end": v(0, 0) * mm, "construction": true});
            skSolve(sketch);
        }
        {
            var Q0;
            Q0=makeQuery(id+"F8.imprint","IMPRINT",FACE,{"disambiguationData":[TD([[makeQuery(id+"F8.imprint","IMPRINT",EDGE,{"derivedFrom":sQuery(id+"F8.wireOp",EDGE,"E43")}),1.0]])]});
            var Q1;
            Q1=sQuery(id+"F8.wireOp",EDGE,"E61");
            revolve(context, id + "F9", {"entities" : qUnion([Q0]), "axis" : qUnion([Q1]), "revolveType" : RevolveType.FULL});
        }
        {
            var Q0;
            Q0=makeQuery(id+"F9.opRevolve","SWEPT_FACE",FACE,{"disambiguationData":[OSD([sQuery(id+"F8.wireOp",EDGE,"E51"),sQuery(id+"F8.wireOp",EDGE,"E57.MirrorCS")])]});
            fillet(context, id + "F10", {"entities" : qUnion([Q0]), "radius" : 11 * mm, "tangentPropagation" : true, "allowEdgeOverflow" : false});
        }
        {
            var Q0;
            Q0=qCreatedBy(makeId("Top.planeOp"),FACE);
            var sketch = newSketch(context, id + "F11", { "sketchPlane" : qUnion([Q0])});
            skCircle(sketch, "E63", {"center": v(0, 0) * mm, "radius": 30 * mm, "construction": true});
            skCircle(sketch, "E64", {"center": v(0, 0) * mm, "radius": 15 * mm, "construction": true});
            skLineSegment(sketch, "E65", {"start": v(0, -15) * mm, "end": v(0, -30) * mm, "construction": true});
            skCircle(sketch, "E66", {"center": v(0, -22.5) * mm, "radius": 7.5 * mm});
            skCircle(sketch, "E67.1.0", {"center": v(21.4, -6.95) * mm, "radius": 7.5 * mm});
            skCircle(sketch, "E67.2.0", {"center": v(13.23, 18.2) * mm, "radius": 7.5 * mm});
            skCircle(sketch, "E67.3.0", {"center": v(-13.23, 18.2) * mm, "radius": 7.5 * mm});
            skCircle(sketch, "E67.4.0", {"center": v(-21.4, -6.95) * mm, "radius": 7.5 * mm});
            skSolve(sketch);
        }
        {
            var Q0;
            Q0 = qSketchRegion(id + "F11", true);
            extrude(context, id + "F12", {"entities" : qUnion([Q0]), "operationType" : NewBodyOperationType.REMOVE, "depth" : 70.3 * mm, "offsetDistance" : 25 * mm});
        }
        {
            var Q0;
            Q0=makeQuery(id+"F9.opRevolve","SWEPT_EDGE",EDGE,{"disambiguationData":[OSD([sQuery(id+"F8.wireOp",EDGE,"E52.MirrorCS"),sQuery(id+"F8.wireOp",EDGE,"E60.MirrorCS")])]});
            var Q1;
            Q1=makeQuery(id+"F9.opRevolve","SWEPT_EDGE",EDGE,{"disambiguationData":[OSD([sQuery(id+"F8.wireOp",EDGE,"E52.MirrorCS"),sQuery(id+"F8.wireOp",EDGE,"E59.MirrorCS")])]});
            fillet(context, id + "F13", {"entities" : qUnion([Q0, Q1]), "radius" : 2 * mm, "tangentPropagation" : true, "allowEdgeOverflow" : false});
        }
    });
